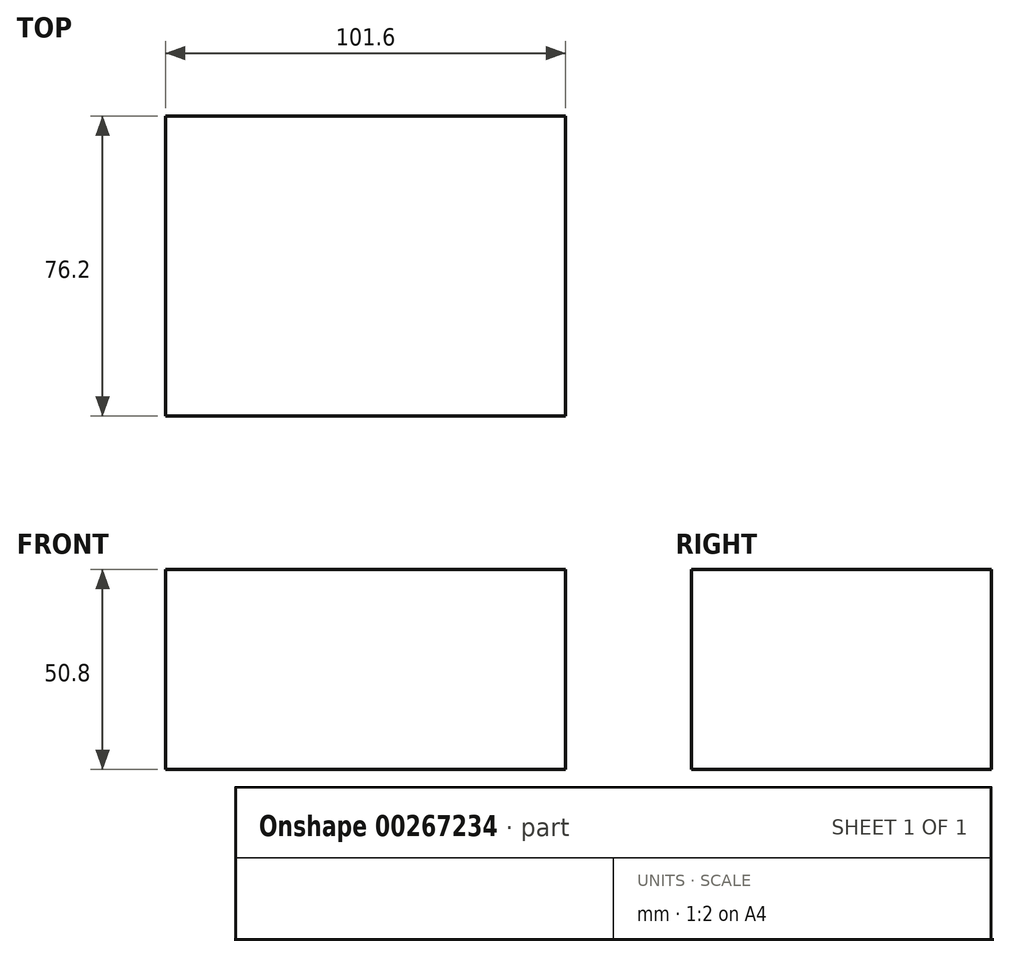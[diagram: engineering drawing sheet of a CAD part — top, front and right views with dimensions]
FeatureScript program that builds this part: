
annotation { "Feature Type Name" : "Feature", "Feature Type Description" : "" }
export const myFeature = defineFeature(function(context is Context, id is Id, definition is map)
    precondition{}
    {
        {
            var Q0;
            Q0=qCreatedBy(makeId("Front.planeOp"),FACE);
            var sketch = newSketch(context, id + "F0", { "sketchPlane" : qUnion([Q0])});
            skLineSegment(sketch, "E0.bottom", {"start": v(0, 0) * mm, "end": v(101.6, 0) * mm});
            skLineSegment(sketch, "E0.top", {"start": v(0, 50.8) * mm, "end": v(101.6, 50.8) * mm});
            skLineSegment(sketch, "E0.left", {"start": v(0, 0) * mm, "end": v(0, 50.8) * mm});
            skLineSegment(sketch, "E0.right", {"start": v(101.6, 0) * mm, "end": v(101.6, 50.8) * mm});
            skSolve(sketch);
        }
        {
            var Q0;
            Q0=makeQuery(id+"F0.imprint","IMPRINT",FACE,{"disambiguationData":[TD([[makeQuery(id+"F0.imprint","IMPRINT",EDGE,{"derivedFrom":sQuery(id+"F0.wireOp",EDGE,"E0.bottom")}),1.0]])]});
            extrude(context, id + "F1", {"entities" : qUnion([Q0]), "depth" : 76.2 * mm});
        }
    });
